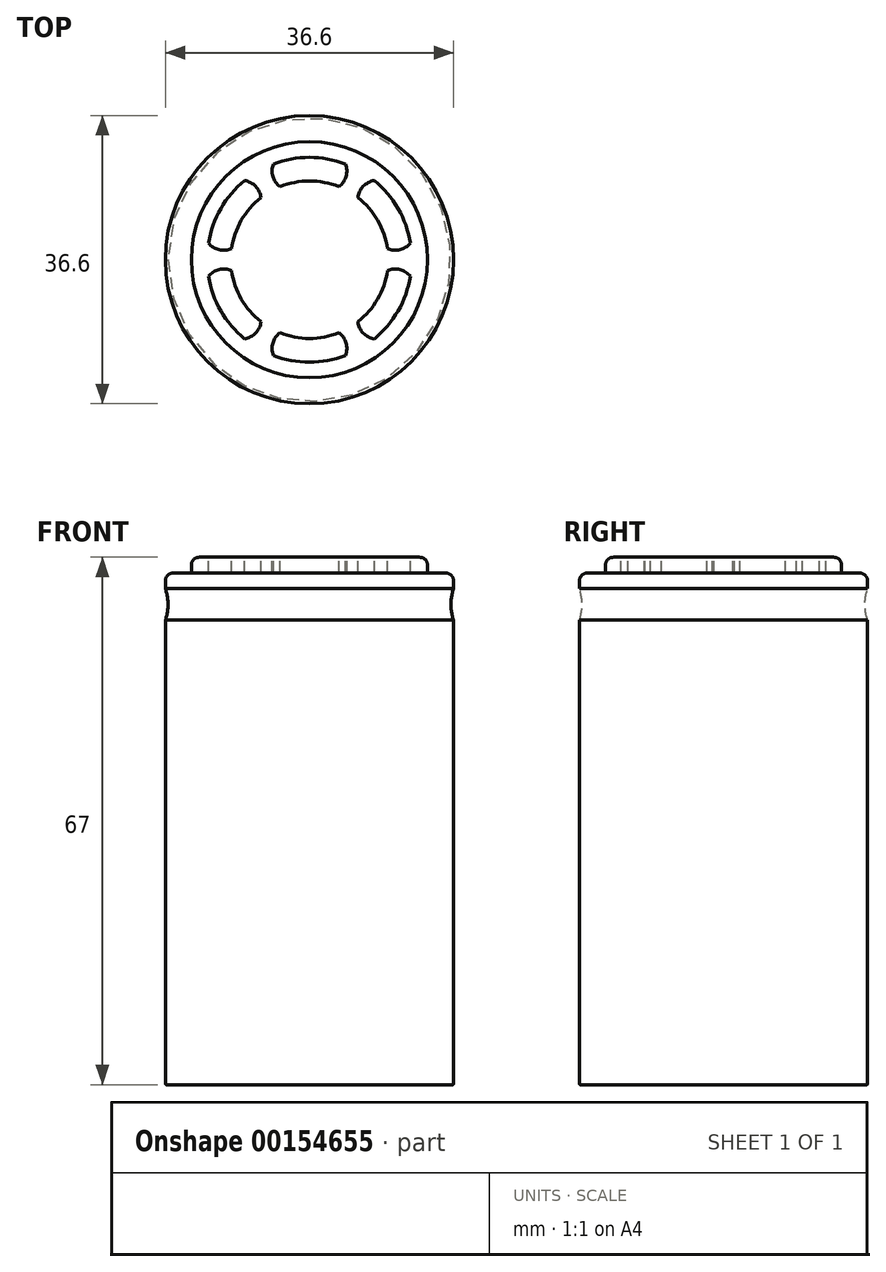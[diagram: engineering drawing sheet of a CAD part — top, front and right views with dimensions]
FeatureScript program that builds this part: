
annotation { "Feature Type Name" : "Feature", "Feature Type Description" : "" }
export const myFeature = defineFeature(function(context is Context, id is Id, definition is map)
    precondition{}
    {
        {
            var Q0;
            Q0=qCreatedBy(makeId("Front.planeOp"),FACE);
            var sketch = newSketch(context, id + "F1", { "sketchPlane" : qUnion([Q0])});
            skLineSegment(sketch, "E0", {"start": v(0, 0) * mm, "end": v(18.2, 0) * mm});
            skLineSegment(sketch, "E1", {"start": v(18.3, 0.1) * mm, "end": v(18.3, 59) * mm});
            skLineSegment(sketch, "E2", {"start": v(17.3, 65) * mm, "end": v(0, 65) * mm});
            skLineSegment(sketch, "E3", {"start": v(0, 65) * mm, "end": v(17.3, 65) * mm});
            skLineSegment(sketch, "E4", {"start": v(18.3, 65) * mm, "end": v(18.3, 65) * mm});
            skLineSegment(sketch, "E5", {"start": v(0, 65) * mm, "end": v(0, 65) * mm});
            skLineSegment(sketch, "E6", {"start": v(0, 67) * mm, "end": v(14, 67) * mm});
            skLineSegment(sketch, "E7", {"start": v(15, 66) * mm, "end": v(15, 65) * mm});
            skArc(sketch, "E8", {"start": v(18.3, 63) * mm, "mid": v(17.98, 61) * mm, "end": v(18.3, 59) * mm});
            skPoint(sketch, "E9.visualSharp", {"position": v(18.3, 65) * mm});
            skArc(sketch, "E9.filletArc", {"start": v(18.3, 64) * mm, "mid": v(18, 64.7) * mm, "end": v(17.3, 65) * mm});
            skPoint(sketch, "E10.visualSharp", {"position": v(18.3, 0) * mm});
            skArc(sketch, "E10.filletArc", {"start": v(18.2, 0) * mm, "mid": v(18.27, 0.03) * mm, "end": v(18.3, 0.1) * mm});
            skPoint(sketch, "E11.visualSharp", {"position": v(15, 67) * mm});
            skArc(sketch, "E11.filletArc", {"start": v(15, 66) * mm, "mid": v(14.7, 66.7) * mm, "end": v(14, 67) * mm});
            skLineSegment(sketch, "E12.trimOffspring", {"start": v(18.3, 63) * mm, "end": v(18.3, 64) * mm});
            skLineSegment(sketch, "E13", {"start": v(0, 67) * mm, "end": v(0, 67) * mm});
            skLineSegment(sketch, "E14", {"start": v(0, 0) * mm, "end": v(0, 67) * mm});
            skSolve(sketch);
        }
        {
            var Q0;
            {var subQ4=sQuery(id+"F1.wireOp",EDGE,"E6");Q0=makeQuery(id+"F1.imprint","IMPRINT",FACE,{"disambiguationData":[TD([[makeQuery(id+"F1.imprint","IMPRINT",EDGE,{"derivedFrom":subQ4}),-1.0]])]});}
            var Q1;
            {var subQ5=sQuery(id+"F1.wireOp",EDGE,"E0");Q1=makeQuery(id+"F1.imprint","IMPRINT",FACE,{"disambiguationData":[TD([[makeQuery(id+"F1.imprint","IMPRINT",EDGE,{"derivedFrom":subQ5}),1.0]])]});}
            var Q2;
            Q2=sQuery(id+"F1.wireOp",EDGE,"E14");
            revolve(context, id + "F2", {"entities" : qUnion([Q0, Q1]), "axis" : qUnion([Q2]), "revolveType" : RevolveType.FULL});
        }
        {
            var Q0;
            Q0=makeQuery(id+"F2.opRevolve","SWEPT_FACE",FACE,{"disambiguationData":[OSD([sQuery(id+"F1.wireOp",EDGE,"E6")])]});
            var sketch = newSketch(context, id + "F3", { "sketchPlane" : qUnion([Q0])});
            skArc(sketch, "E15", {"start": v(3.74, 9.27) * mm, "mid": v(0, 10) * mm, "end": v(-3.74, 9.27) * mm});
            skArc(sketch, "E16", {"start": v(4.59, 12.16) * mm, "mid": v(0, 13) * mm, "end": v(-4.59, 12.16) * mm});
            skArc(sketch, "E17", {"start": v(3.74, 9.27) * mm, "mid": v(4.65, 10.58) * mm, "end": v(4.59, 12.16) * mm});
            skArc(sketch, "E18", {"start": v(-4.59, 12.16) * mm, "mid": v(-4.65, 10.58) * mm, "end": v(-3.74, 9.27) * mm});
            skPoint(sketch, "E19.start.orphan", {"position": v(0, -14) * mm});
            skArc(sketch, "E20.1.0", {"start": v(12.83, 2.1) * mm, "mid": v(11.26, 6.5) * mm, "end": v(8.24, 10.05) * mm});
            skArc(sketch, "E20.1.1", {"start": v(9.9, 1.4) * mm, "mid": v(8.66, 5) * mm, "end": v(6.16, 7.88) * mm});
            skArc(sketch, "E20.1.2", {"start": v(9.9, 1.4) * mm, "mid": v(11.48, 1.26) * mm, "end": v(12.83, 2.1) * mm});
            skArc(sketch, "E20.1.3", {"start": v(8.24, 10.05) * mm, "mid": v(6.83, 9.32) * mm, "end": v(6.16, 7.88) * mm});
            skArc(sketch, "E20.2.0", {"start": v(8.24, -10.05) * mm, "mid": v(11.26, -6.5) * mm, "end": v(12.83, -2.1) * mm});
            skArc(sketch, "E20.2.1", {"start": v(6.16, -7.88) * mm, "mid": v(8.66, -5) * mm, "end": v(9.9, -1.4) * mm});
            skArc(sketch, "E20.2.2", {"start": v(6.16, -7.88) * mm, "mid": v(6.83, -9.32) * mm, "end": v(8.24, -10.05) * mm});
            skArc(sketch, "E20.2.3", {"start": v(12.83, -2.1) * mm, "mid": v(11.48, -1.26) * mm, "end": v(9.9, -1.4) * mm});
            skArc(sketch, "E20.3.0", {"start": v(-4.59, -12.16) * mm, "mid": v(0, -13) * mm, "end": v(4.59, -12.16) * mm});
            skArc(sketch, "E20.3.1", {"start": v(-3.74, -9.27) * mm, "mid": v(0, -10) * mm, "end": v(3.74, -9.27) * mm});
            skArc(sketch, "E20.3.2", {"start": v(-3.74, -9.27) * mm, "mid": v(-4.65, -10.58) * mm, "end": v(-4.59, -12.16) * mm});
            skArc(sketch, "E20.3.3", {"start": v(4.59, -12.16) * mm, "mid": v(4.65, -10.58) * mm, "end": v(3.74, -9.27) * mm});
            skArc(sketch, "E20.4.0", {"start": v(-12.83, -2.1) * mm, "mid": v(-11.26, -6.5) * mm, "end": v(-8.24, -10.05) * mm});
            skArc(sketch, "E20.4.1", {"start": v(-9.9, -1.4) * mm, "mid": v(-8.66, -5) * mm, "end": v(-6.16, -7.88) * mm});
            skArc(sketch, "E20.4.2", {"start": v(-9.9, -1.4) * mm, "mid": v(-11.48, -1.26) * mm, "end": v(-12.83, -2.1) * mm});
            skArc(sketch, "E20.4.3", {"start": v(-8.24, -10.05) * mm, "mid": v(-6.83, -9.32) * mm, "end": v(-6.16, -7.88) * mm});
            skArc(sketch, "E20.5.0", {"start": v(-8.24, 10.05) * mm, "mid": v(-11.26, 6.5) * mm, "end": v(-12.83, 2.1) * mm});
            skArc(sketch, "E20.5.1", {"start": v(-6.16, 7.88) * mm, "mid": v(-8.66, 5) * mm, "end": v(-9.9, 1.4) * mm});
            skArc(sketch, "E20.5.2", {"start": v(-6.16, 7.88) * mm, "mid": v(-6.83, 9.32) * mm, "end": v(-8.24, 10.05) * mm});
            skArc(sketch, "E20.5.3", {"start": v(-12.83, 2.1) * mm, "mid": v(-11.48, 1.26) * mm, "end": v(-9.9, 1.4) * mm});
            skLineSegment(sketch, "E20.anchor1", {"start": v(0, 0) * mm, "end": v(-4.59, 12.16) * mm, "construction": true});
            skLineSegment(sketch, "E20.anchor2", {"start": v(0, 0) * mm, "end": v(-12.83, 2.1) * mm, "construction": true});
            skSolve(sketch);
        }
        {
            var Q0;
            Q0=makeQuery(id+"F3.imprint","IMPRINT",FACE,{"disambiguationData":[TD([[makeQuery(id+"F3.imprint","IMPRINT",EDGE,{"derivedFrom":sQuery(id+"F3.wireOp",EDGE,"E20.5.0")}),1.0]])]});
            var Q1;
            Q1=makeQuery(id+"F3.imprint","IMPRINT",FACE,{"disambiguationData":[TD([[makeQuery(id+"F3.imprint","IMPRINT",EDGE,{"derivedFrom":sQuery(id+"F3.wireOp",EDGE,"E15")}),-1.0]])]});
            var Q2;
            Q2=makeQuery(id+"F3.imprint","IMPRINT",FACE,{"disambiguationData":[TD([[makeQuery(id+"F3.imprint","IMPRINT",EDGE,{"derivedFrom":sQuery(id+"F3.wireOp",EDGE,"E20.4.0")}),1.0]])]});
            var Q3;
            Q3=makeQuery(id+"F3.imprint","IMPRINT",FACE,{"disambiguationData":[TD([[makeQuery(id+"F3.imprint","IMPRINT",EDGE,{"derivedFrom":sQuery(id+"F3.wireOp",EDGE,"E20.3.0")}),1.0]])]});
            var Q4;
            Q4=makeQuery(id+"F3.imprint","IMPRINT",FACE,{"disambiguationData":[TD([[makeQuery(id+"F3.imprint","IMPRINT",EDGE,{"derivedFrom":sQuery(id+"F3.wireOp",EDGE,"E20.2.0")}),1.0]])]});
            var Q5;
            Q5=makeQuery(id+"F3.imprint","IMPRINT",FACE,{"disambiguationData":[TD([[makeQuery(id+"F3.imprint","IMPRINT",EDGE,{"derivedFrom":sQuery(id+"F3.wireOp",EDGE,"E20.1.0")}),1.0]])]});
            extrude(context, id + "F4", {"entities" : qUnion([Q0, Q1, Q2, Q3, Q4, Q5]), "operationType" : NewBodyOperationType.REMOVE, "oppositeDirection" : true, "depth" : 2 * mm});
        }
        {
            var Q0;
            {var subQ4=sQuery(id+"F1.wireOp",EDGE,"E6");Q0=makeQuery(id+"F1.imprint","IMPRINT",FACE,{"disambiguationData":[TD([[makeQuery(id+"F1.imprint","IMPRINT",EDGE,{"derivedFrom":subQ4}),-1.0]])]});}
            var Q1;
            {var subQ5=sQuery(id+"F1.wireOp",EDGE,"E0");Q1=makeQuery(id+"F1.imprint","IMPRINT",FACE,{"disambiguationData":[TD([[makeQuery(id+"F1.imprint","IMPRINT",EDGE,{"derivedFrom":subQ5}),1.0]])]});}
            var Q2;
            Q2=sQuery(id+"F1.wireOp",EDGE,"E14");
            revolve(context, id + "F0", {"entities" : qUnion([Q0, Q1]), "axis" : qUnion([Q2]), "revolveType" : RevolveType.FULL});
        }
    });
